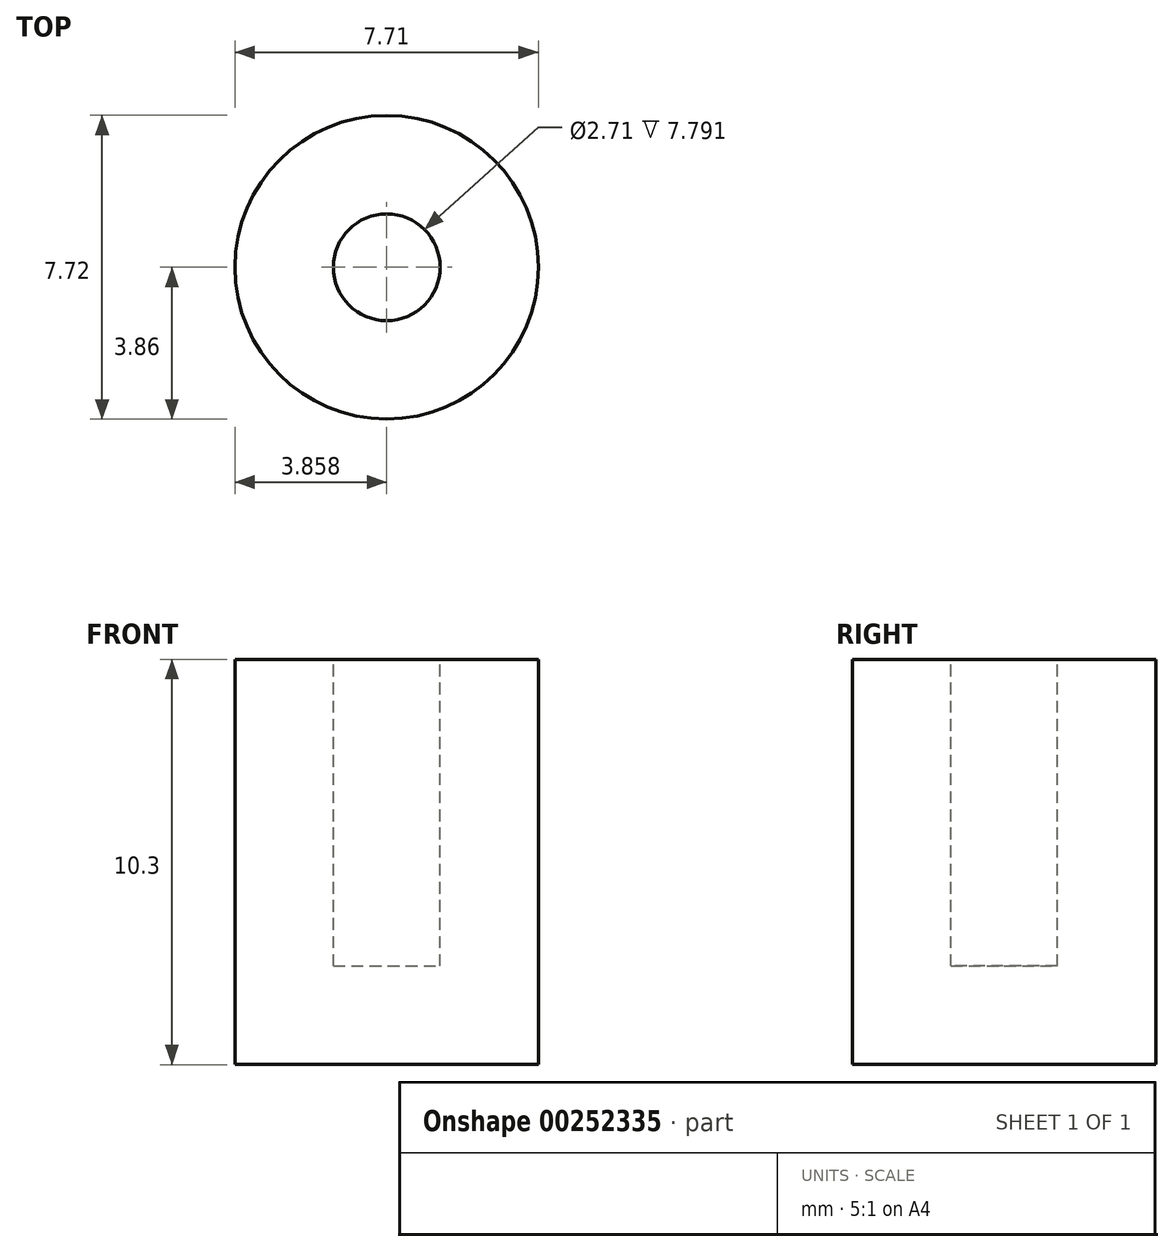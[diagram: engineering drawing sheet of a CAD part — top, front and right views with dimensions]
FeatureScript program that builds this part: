
annotation { "Feature Type Name" : "Feature", "Feature Type Description" : "" }
export const myFeature = defineFeature(function(context is Context, id is Id, definition is map)
    precondition{}
    {
        {
            var Q0;
            Q0=qCreatedBy(makeId("Front.planeOp"),FACE);
            var sketch = newSketch(context, id + "F0", { "sketchPlane" : qUnion([Q0])});
            skLineSegment(sketch, "E0.bottom", {"start": v(-1.93, 5.15) * mm, "end": v(1.93, 5.15) * mm});
            skLineSegment(sketch, "E0.top", {"start": v(-1.93, -5.15) * mm, "end": v(1.93, -5.15) * mm});
            skLineSegment(sketch, "E0.left", {"start": v(-1.93, 5.15) * mm, "end": v(-1.93, -5.15) * mm});
            skLineSegment(sketch, "E0.right", {"start": v(1.93, 5.15) * mm, "end": v(1.93, -5.15) * mm});
            skPoint(sketch, "E0.middle", {"position": v(0, 0) * mm});
            skSolve(sketch);
        }
        {
            var Q0;
            Q0 = qSketchRegion(id + "F0", true);
            var Q1;
            Q1=sQuery(id+"F0.wireOp",EDGE,"E0.right");
            revolve(context, id + "F1", {"entities" : qUnion([Q0]), "axis" : qUnion([Q1]), "revolveType" : RevolveType.FULL});
        }
        {
            var Q0;
            Q0=makeQuery(id+"F1.opRevolve","SWEPT_FACE",FACE,{"disambiguationData":[OSD([sQuery(id+"F0.wireOp",EDGE,"E0.bottom")])]});
            shell(context, id + "F2", {"entities" : qUnion([Q0]), "thickness" : 2.5 * mm});
        }
    });
